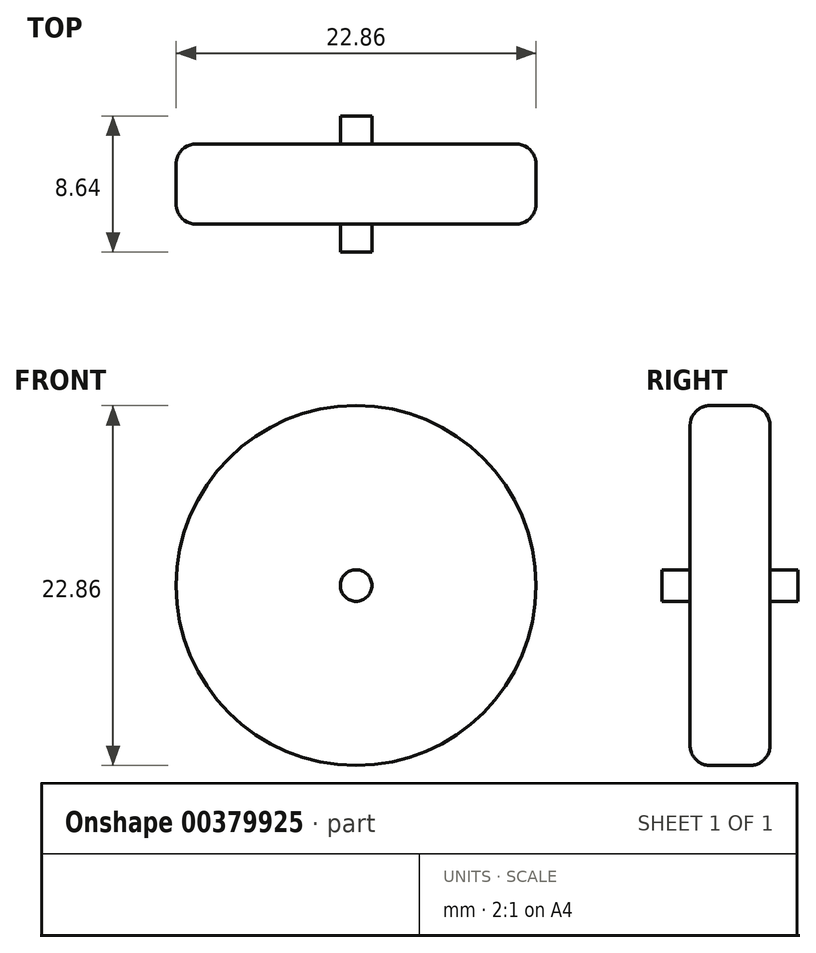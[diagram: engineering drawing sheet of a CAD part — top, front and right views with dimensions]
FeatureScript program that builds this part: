
annotation { "Feature Type Name" : "Feature", "Feature Type Description" : "" }
export const myFeature = defineFeature(function(context is Context, id is Id, definition is map)
    precondition{}
    {
        {
            var Q0;
            Q0=qCreatedBy(makeId("Front.planeOp"),FACE);
            var sketch = newSketch(context, id + "F0", { "sketchPlane" : qUnion([Q0])});
            skCircle(sketch, "E0", {"center": v(0, 0) * mm, "radius": 1 * mm});
            skCircle(sketch, "E1", {"center": v(0, 0) * mm, "radius": 11.43 * mm});
            skSolve(sketch);
        }
        {
            var Q0;
            Q0=makeQuery(id+"F0.imprint","IMPRINT",FACE,{"disambiguationData":[TD([[makeQuery(id+"F0.imprint","IMPRINT",EDGE,{"derivedFrom":sQuery(id+"F0.wireOp",EDGE,"E0")}),1.0]])]});
            extrude(context, id + "F1", {"entities" : qUnion([Q0]), "depth" : 4.32 * mm, "hasSecondDirection" : true, "secondDirectionOppositeDirection" : true, "secondDirectionDepth" : 4.32 * mm});
        }
        {
            var Q0;
            Q0 = qSketchRegion(id + "F0", true);
            extrude(context, id + "F2", {"entities" : qUnion([Q0]), "operationType" : NewBodyOperationType.ADD, "depth" : 2.54 * mm, "hasSecondDirection" : true, "secondDirectionOppositeDirection" : true, "secondDirectionDepth" : 2.54 * mm});
        }
        {
            var Q0;
            Q0=makeQuery(id+"F2.opExtrude","CAP_EDGE",EDGE,{"disambiguationData":[OSD([sQuery(id+"F0.wireOp",EDGE,"E1")])],"isStart":false});
            var Q1;
            Q1=makeQuery(id+"F2.opExtrude","CAP_EDGE",EDGE,{"disambiguationData":[OSD([sQuery(id+"F0.wireOp",EDGE,"E1")])],"isStart":true});
            fillet(context, id + "F3", {"entities" : qUnion([Q0, Q1]), "radius" : 1.27 * mm, "tangentPropagation" : true, "allowEdgeOverflow" : false});
        }
    });
